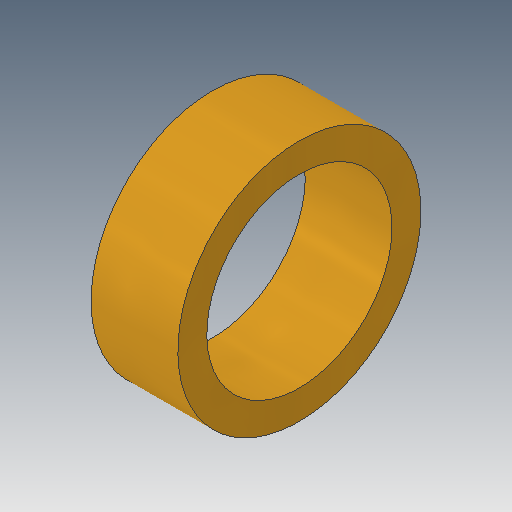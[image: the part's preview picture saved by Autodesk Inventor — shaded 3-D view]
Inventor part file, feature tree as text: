
AUTODESK INVENTOR PART (.ipt)
format: ipt  version: 2019.4 (Build 234330000, 330)  size: 105,472 bytes
history: native  units: mm
features: other x1, extrude x1, sketch x1
ambient origin geometry x8: Origin, YZ Plane, XZ Plane, XY Plane, X Axis, Y Axis, Z Axis, Center Point
bodies: Body1 (feature_tree)
feature tree (3):
  other  "ソリッド1"
  extrude  "押し出し1"  Depth=4.2mm
  sketch  "スケッチ1"
